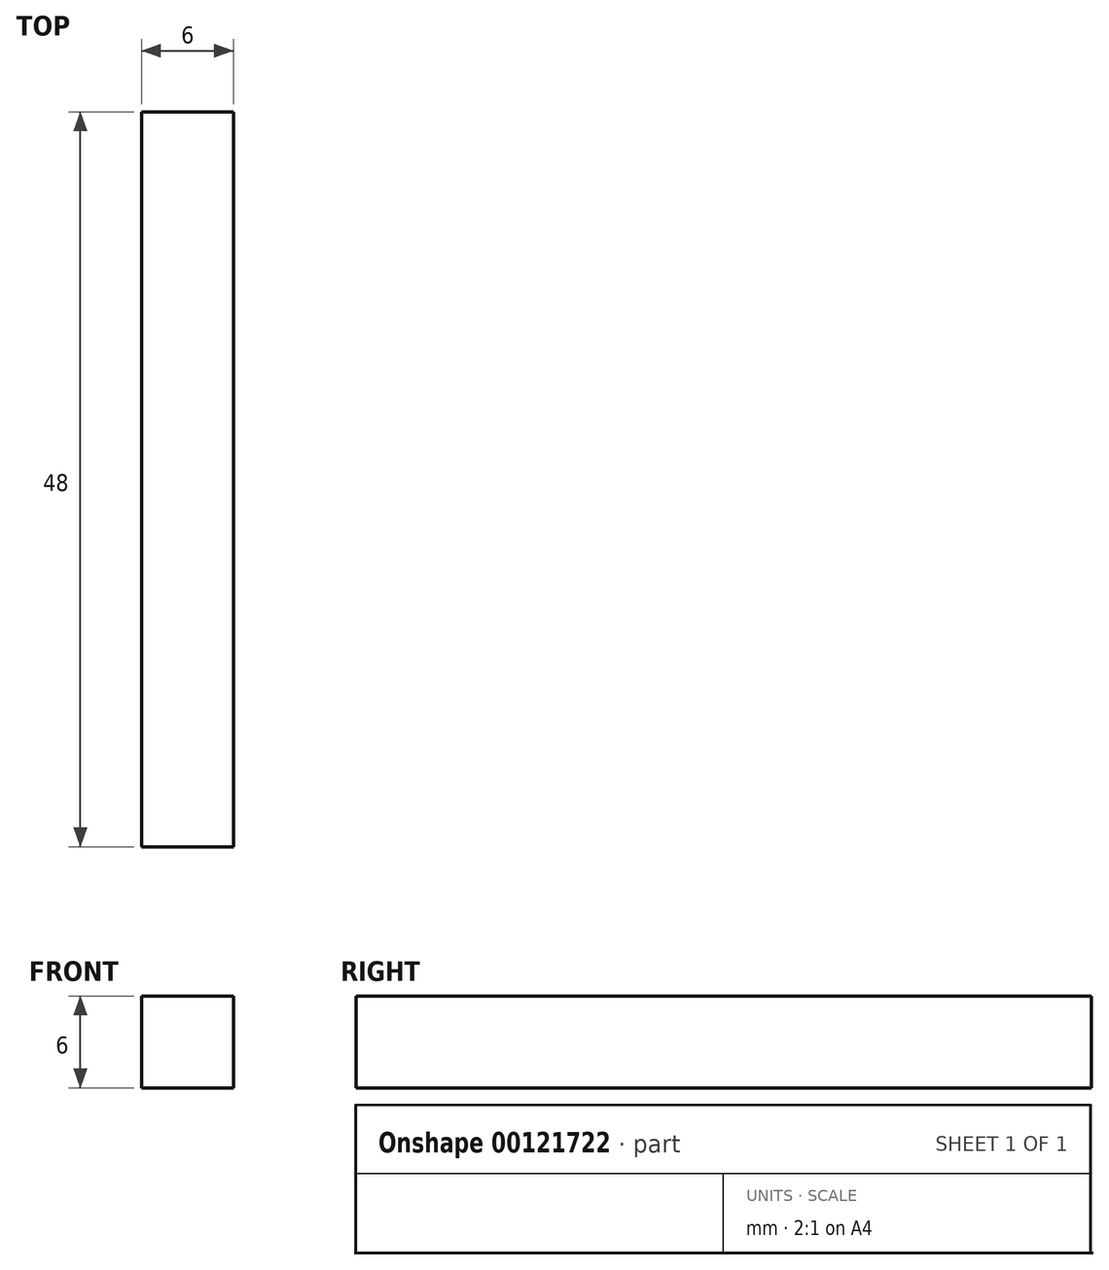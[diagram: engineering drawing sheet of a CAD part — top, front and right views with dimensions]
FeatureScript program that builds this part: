
annotation { "Feature Type Name" : "Feature", "Feature Type Description" : "" }
export const myFeature = defineFeature(function(context is Context, id is Id, definition is map)
    precondition{}
    {
        {
            var Q0;
            Q0=qCreatedBy(makeId("Front.planeOp"),FACE);
            var sketch = newSketch(context, id + "F0", { "sketchPlane" : qUnion([Q0])});
            skLineSegment(sketch, "E0.bottom", {"start": v(0, 0) * mm, "end": v(6, 0) * mm});
            skLineSegment(sketch, "E0.top", {"start": v(0, 6) * mm, "end": v(6, 6) * mm});
            skLineSegment(sketch, "E0.left", {"start": v(0, 0) * mm, "end": v(0, 6) * mm});
            skLineSegment(sketch, "E0.right", {"start": v(6, 0) * mm, "end": v(6, 6) * mm});
            skSolve(sketch);
        }
        {
            assignVariable(context, id + "F1", {"name" : "connectorLength", "anyValue" : 48});
        }
        {
            var Q0;
            Q0=makeQuery(id+"F0.imprint","IMPRINT",FACE,{"disambiguationData":[TD([[makeQuery(id+"F0.imprint","IMPRINT",EDGE,{"derivedFrom":sQuery(id+"F0.wireOp",EDGE,"E0.bottom")}),1.0]])]});
            extrude(context, id + "F2", {"entities" : qUnion([Q0]), "depth" : (getVariable(context, 'connectorLength')) * mm});
        }
    });
